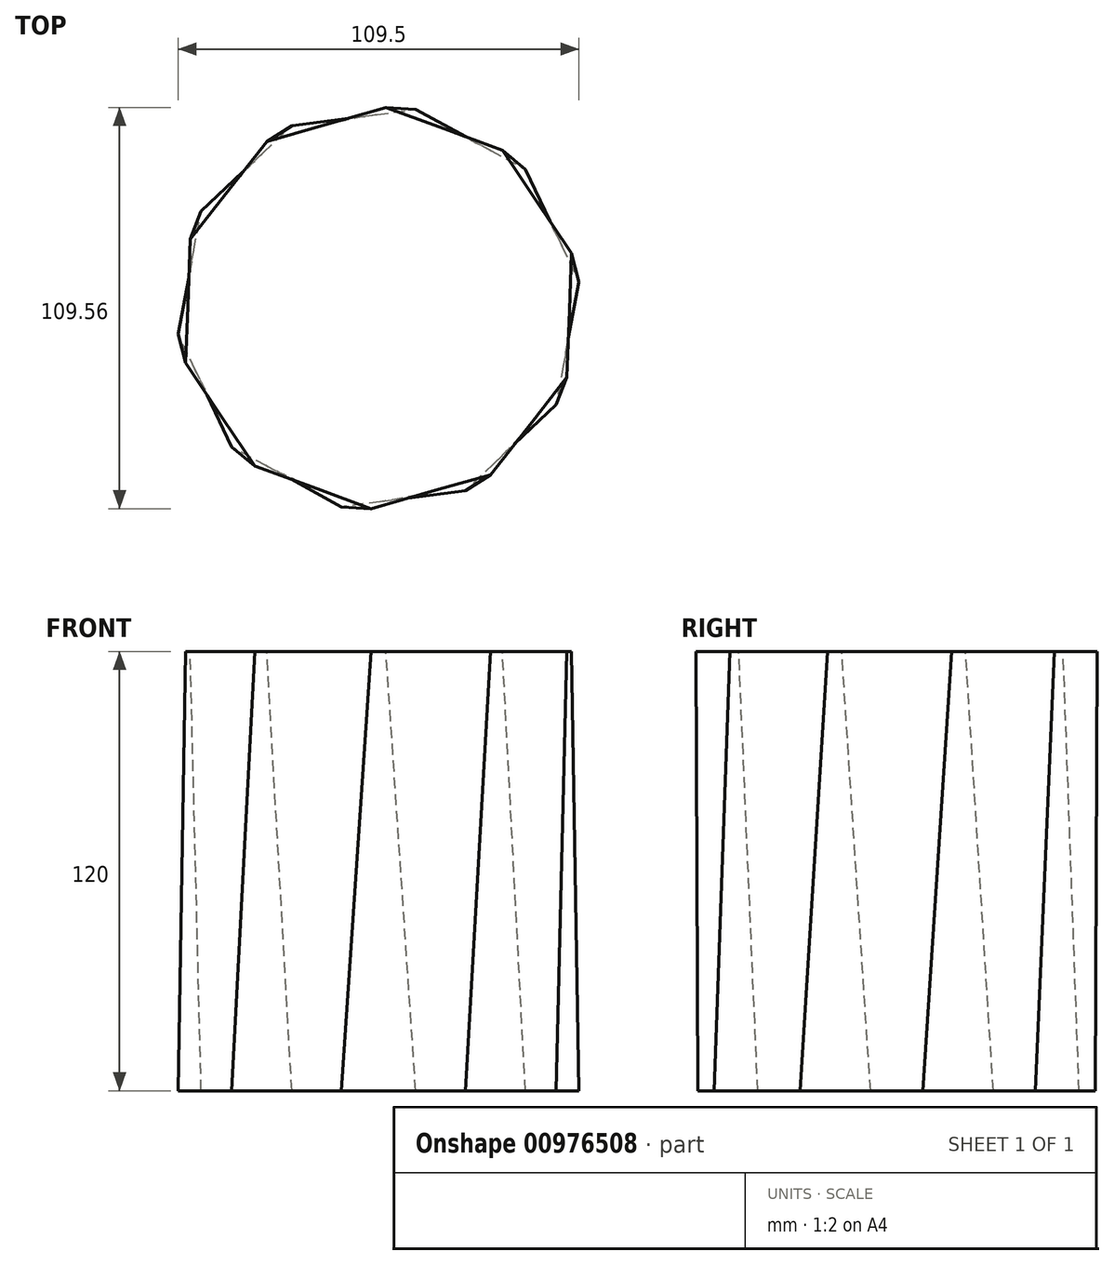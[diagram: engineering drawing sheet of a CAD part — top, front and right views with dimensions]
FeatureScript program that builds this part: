
annotation { "Feature Type Name" : "Feature", "Feature Type Description" : "" }
export const myFeature = defineFeature(function(context is Context, id is Id, definition is map)
    precondition{}
    {
        {
            var Q0;
            Q0=qCreatedBy(makeId("Top.planeOp"),FACE);
            var sketch = newSketch(context, id + "F0", { "sketchPlane" : qUnion([Q0])});
            skCircle(sketch, "E0.cCircle", {"center": v(0, 0) * mm, "radius": 52.5 * mm, "construction": true});
            skLineSegment(sketch, "E0.0", {"start": v(23.69, -49.87) * mm, "end": v(-10.15, -54.27) * mm});
            skLineSegment(sketch, "E0.1", {"start": v(-10.15, -54.27) * mm, "end": v(-40.1, -37.94) * mm});
            skLineSegment(sketch, "E0.2", {"start": v(-40.1, -37.94) * mm, "end": v(-54.75, -7.12) * mm});
            skLineSegment(sketch, "E0.3", {"start": v(-54.75, -7.12) * mm, "end": v(-48.47, 26.42) * mm});
            skLineSegment(sketch, "E0.4", {"start": v(-48.47, 26.42) * mm, "end": v(-23.69, 49.87) * mm});
            skLineSegment(sketch, "E0.5", {"start": v(-23.69, 49.87) * mm, "end": v(10.15, 54.27) * mm});
            skLineSegment(sketch, "E0.6", {"start": v(10.15, 54.27) * mm, "end": v(40.1, 37.94) * mm});
            skLineSegment(sketch, "E0.7", {"start": v(40.1, 37.94) * mm, "end": v(54.75, 7.12) * mm});
            skLineSegment(sketch, "E0.8", {"start": v(54.75, 7.12) * mm, "end": v(48.47, -26.42) * mm});
            skLineSegment(sketch, "E0.9", {"start": v(48.47, -26.42) * mm, "end": v(23.69, -49.87) * mm});
            skPoint(sketch, "E0.0.midPoint", {"position": v(6.77, -52.07) * mm});
            skSolve(sketch);
        }
        {
            var Q0;
            Q0=qCreatedBy(makeId("Top.planeOp"),FACE);
            cPlane(context, id + "F1", {"entities" : qUnion([Q0]), "cplaneType" : CPlaneType.OFFSET, "offset" : 58 * mm, "width" : 150 * mm, "height" : 150 * mm});
        }
        {
            var Q0;
            Q0=qCreatedBy(makeId("Top.planeOp"),FACE);
            cPlane(context, id + "F2", {"entities" : qUnion([Q0]), "cplaneType" : CPlaneType.OFFSET, "offset" : 120 * mm, "width" : 150 * mm, "height" : 150 * mm});
        }
        {
            var Q0;
            Q0=qCreatedBy(id+"F2.planeOp",FACE);
            var sketch = newSketch(context, id + "F3", { "sketchPlane" : qUnion([Q0])});
            skCircle(sketch, "E1.cCircle", {"center": v(0, 0) * mm, "radius": 52.13 * mm, "construction": true});
            skLineSegment(sketch, "E1.0", {"start": v(30.55, -45.5) * mm, "end": v(-2.03, -54.78) * mm});
            skLineSegment(sketch, "E1.1", {"start": v(-2.03, -54.78) * mm, "end": v(-33.84, -43.12) * mm});
            skLineSegment(sketch, "E1.2", {"start": v(-33.84, -43.12) * mm, "end": v(-52.72, -15) * mm});
            skLineSegment(sketch, "E1.3", {"start": v(-52.72, -15) * mm, "end": v(-51.47, 18.86) * mm});
            skLineSegment(sketch, "E1.4", {"start": v(-51.47, 18.86) * mm, "end": v(-30.55, 45.5) * mm});
            skLineSegment(sketch, "E1.5", {"start": v(-30.55, 45.5) * mm, "end": v(2.03, 54.78) * mm});
            skLineSegment(sketch, "E1.6", {"start": v(2.03, 54.78) * mm, "end": v(33.84, 43.12) * mm});
            skLineSegment(sketch, "E1.7", {"start": v(33.84, 43.12) * mm, "end": v(52.72, 15) * mm});
            skLineSegment(sketch, "E1.8", {"start": v(52.72, 15) * mm, "end": v(51.47, -18.86) * mm});
            skLineSegment(sketch, "E1.9", {"start": v(51.47, -18.86) * mm, "end": v(30.55, -45.5) * mm});
            skPoint(sketch, "E1.0.midPoint", {"position": v(14.26, -50.14) * mm});
            skSolve(sketch);
        }
        {
            var Q0;
            Q0=makeQuery(id+"F0.imprint","IMPRINT",FACE,{"disambiguationData":[TD([[makeQuery(id+"F0.imprint","IMPRINT",EDGE,{"derivedFrom":sQuery(id+"F0.wireOp",EDGE,"E0.0")}),-1.0]])]});
            var Q1;
            Q1=makeQuery(id+"F3.imprint","IMPRINT",FACE,{"disambiguationData":[TD([[makeQuery(id+"F3.imprint","IMPRINT",EDGE,{"derivedFrom":sQuery(id+"F3.wireOp",EDGE,"E1.0")}),-1.0]])]});
            loft(context, id + "F4", {"sheetProfilesArray" : [{ "sheetProfileEntities" : qUnion([Q0]) }, { "sheetProfileEntities" : qUnion([Q1]) }]});
        }
    });
